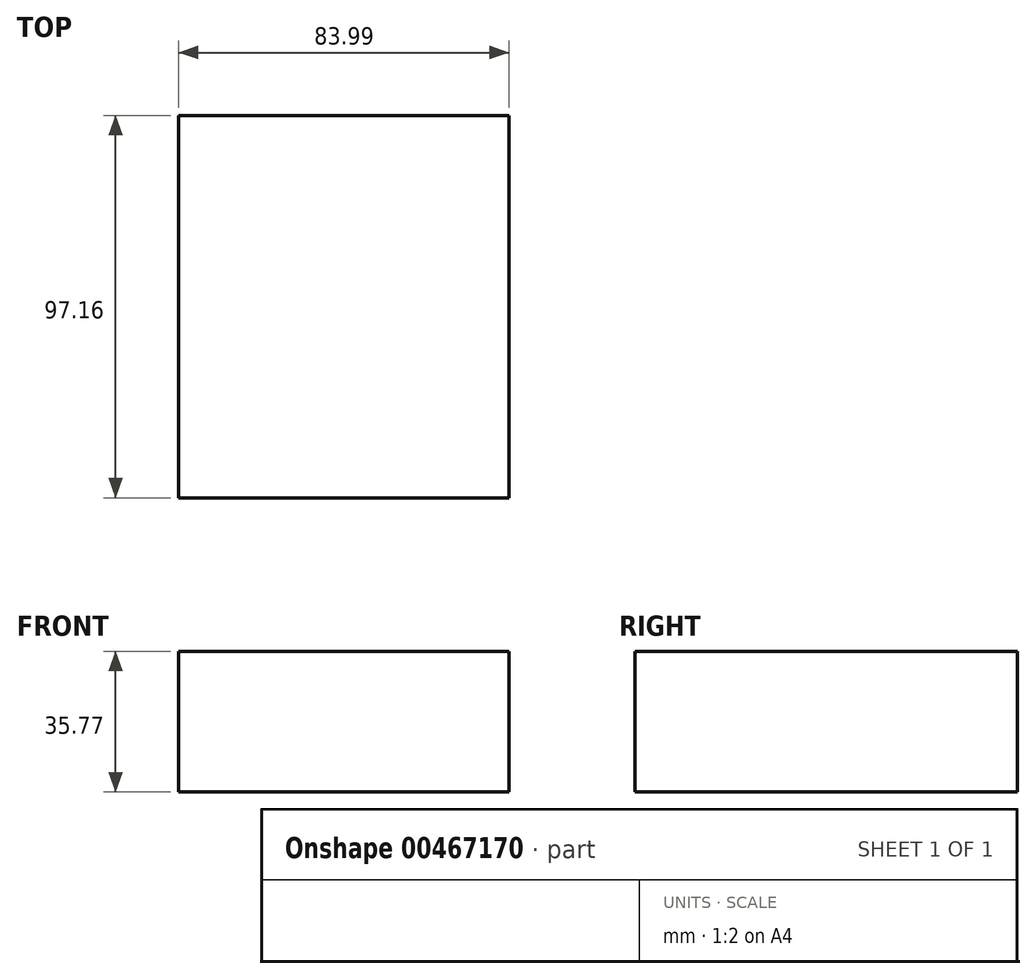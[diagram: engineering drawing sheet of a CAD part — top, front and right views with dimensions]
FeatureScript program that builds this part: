
annotation { "Feature Type Name" : "Feature", "Feature Type Description" : "" }
export const myFeature = defineFeature(function(context is Context, id is Id, definition is map)
    precondition{}
    {
        {
            var Q0;
            Q0=qCreatedBy(makeId("Front.planeOp"),FACE);
            var sketch = newSketch(context, id + "F0", { "sketchPlane" : qUnion([Q0])});
            skLineSegment(sketch, "E0.bottom", {"start": v(-40.75, -7.92) * mm, "end": v(43.24, -7.92) * mm});
            skLineSegment(sketch, "E0.top", {"start": v(-40.75, 27.85) * mm, "end": v(43.24, 27.85) * mm});
            skLineSegment(sketch, "E0.left", {"start": v(-40.75, -7.92) * mm, "end": v(-40.75, 27.85) * mm});
            skLineSegment(sketch, "E0.right", {"start": v(43.24, -7.92) * mm, "end": v(43.24, 27.85) * mm});
            skSolve(sketch);
        }
        {
            var Q0;
            Q0 = qSketchRegion(id + "F0", true);
            extrude(context, id + "F1", {"entities" : qUnion([Q0]), "depth" : 97.16 * mm});
        }
        {
            var Q0;
            Q0=makeQuery(id+"F1.opExtrude","SWEPT_FACE",FACE,{"disambiguationData":[OSD([sQuery(id+"F0.wireOp",EDGE,"E0.top")])]});
            var sketch = newSketch(context, id + "F2", { "sketchPlane" : qUnion([Q0])});
            skCircle(sketch, "E1", {"center": v(16.65, -45.04) * mm, "radius": 22.4 * mm});
            skSolve(sketch);
        }
        {
            var Q0;
            Q0=sQuery(id+"F2.wireOp",EDGE,"E1");
            extrude(context, id + "F3", {"bodyType" : ToolBodyType.SURFACE, "surfaceEntities" : qUnion([Q0]), "depth" : 25.4 * mm, "offsetDistance" : 25.4 * mm});
        }
    });
